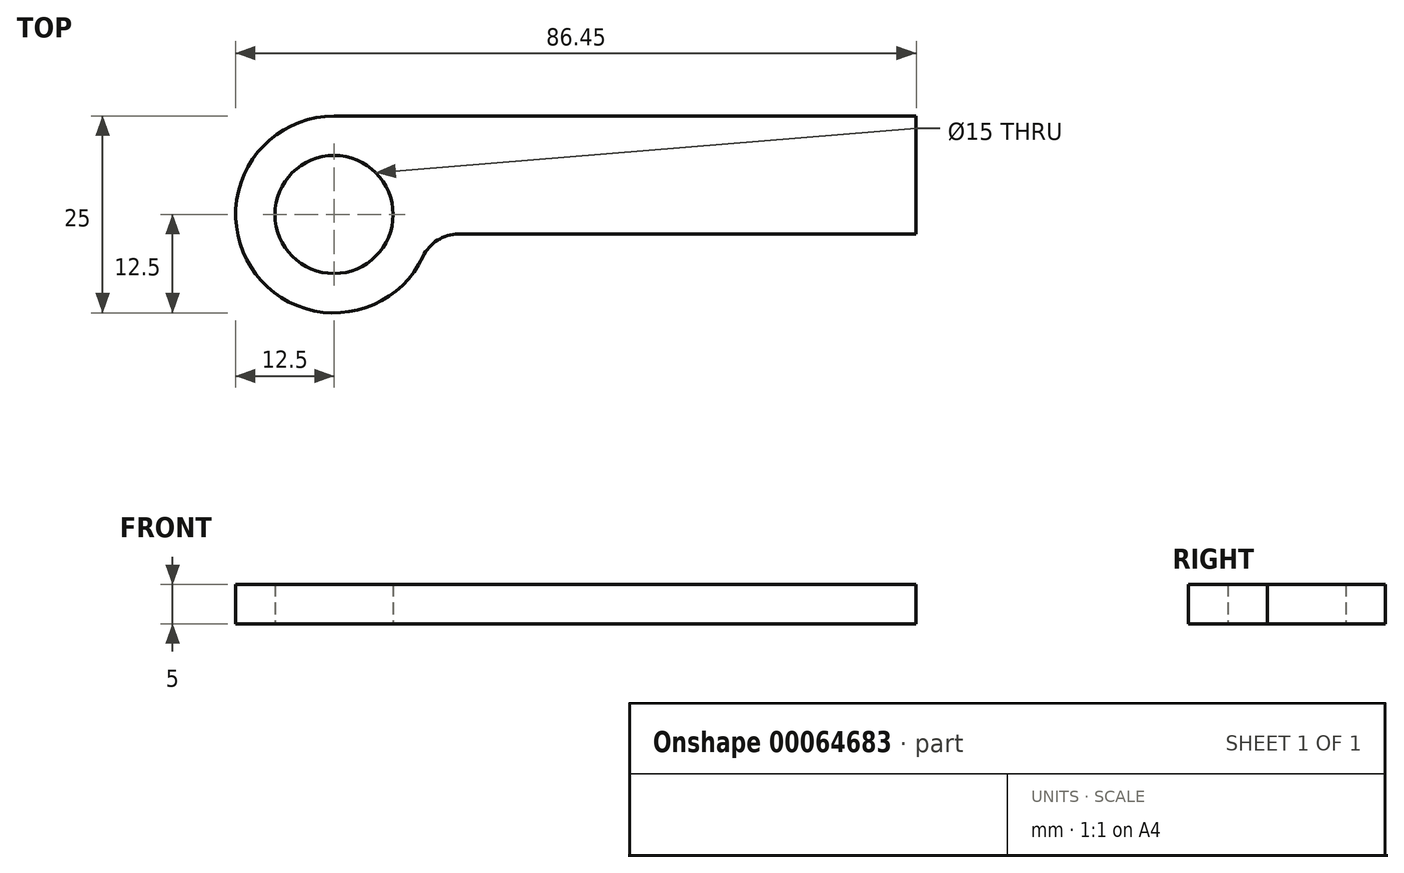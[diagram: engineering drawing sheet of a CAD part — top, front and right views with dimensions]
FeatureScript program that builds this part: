
annotation { "Feature Type Name" : "Feature", "Feature Type Description" : "" }
export const myFeature = defineFeature(function(context is Context, id is Id, definition is map)
    precondition{}
    {
        {
            var Q0;
            Q0=qCreatedBy(makeId("Top.planeOp"),FACE);
            var sketch = newSketch(context, id + "F0", { "sketchPlane" : qUnion([Q0])});
            skLineSegment(sketch, "E0.bottom", {"start": v(-21.74, 25) * mm, "end": v(52.2, 25) * mm});
            skLineSegment(sketch, "E0.right", {"start": v(52.2, 25) * mm, "end": v(52.2, 10) * mm});
            skLineSegment(sketch, "E1", {"start": v(-21.67, 0) * mm, "end": v(-21.74, 0) * mm});
            skArc(sketch, "E2", {"start": v(-21.74, 25) * mm, "mid": v(-32.3, 5.82) * mm, "end": v(-10.45, 7.14) * mm});
            skLineSegment(sketch, "E3", {"start": v(52.2, 10) * mm, "end": v(-5.93, 10) * mm});
            skPoint(sketch, "E4.visualSharp", {"position": v(-9.5, 10) * mm});
            skArc(sketch, "E4.filletArc", {"start": v(-5.93, 10) * mm, "mid": v(-8.6, 9.23) * mm, "end": v(-10.45, 7.14) * mm});
            skCircle(sketch, "E5", {"center": v(-21.74, 12.5) * mm, "radius": 7.5 * mm});
            skLineSegment(sketch, "E6", {"start": v(28.01, 0) * mm, "end": v(28.01, 0) * mm});
            skPoint(sketch, "E7.newPointB", {"position": v(28.01, 10) * mm});
            skSolve(sketch);
        }
        {
            var Q0;
            Q0 = qSketchRegion(id + "F0", true);
            extrude(context, id + "F1", {"entities" : qUnion([Q0]), "depth" : 5 * mm});
        }
    });
